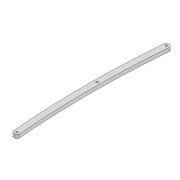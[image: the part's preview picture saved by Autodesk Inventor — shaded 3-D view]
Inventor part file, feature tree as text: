
AUTODESK INVENTOR PART (.ipt)
format: ipt  version: 2022 (Build 260153000, 153)  size: 96,256 bytes
history: native  units: mm
features: extrude x1
ambient origin geometry x8: Origin, YZ Plane, XZ Plane, XY Plane, X Axis, Y Axis, Z Axis, Center Point
bodies: Solid1 (feature_tree)
feature tree (1):
  extrude  "Extrusion1"  Depth=3.3mm
